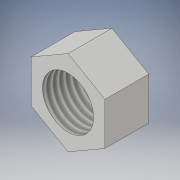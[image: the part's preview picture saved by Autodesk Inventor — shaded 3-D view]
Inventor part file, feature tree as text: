
AUTODESK INVENTOR PART (.ipt)
format: ipt  version: 2017 (Build 210142000, 142)  size: 102,912 bytes
history: native  units: in
note: dims shown in document units (in); Inventor stores cm internally (conversion verified against a paired STEP export)
features: extrude x1, thread x1, sketch x1
ambient origin geometry x8: Origin, YZ Plane, XZ Plane, XY Plane, X Axis, Y Axis, Z Axis, Center Point
bodies: Solid1 (feature_tree)
feature tree (3):
  extrude  "Extrusion1"  Depth=0.75in TaperAngle=0.0deg
  thread  "Thread1"  [1 undecoded]
  sketch  "Sketch1"  dims[d0=0.875in d1=0.75in d2=0.0in d3=1.0in d4=0.0in]
note: 1 required parameter value undecoded (feature->parameter linkage not recoverable at this tier; creation-order binding heuristic only, values carry confidence <= 0.55)
